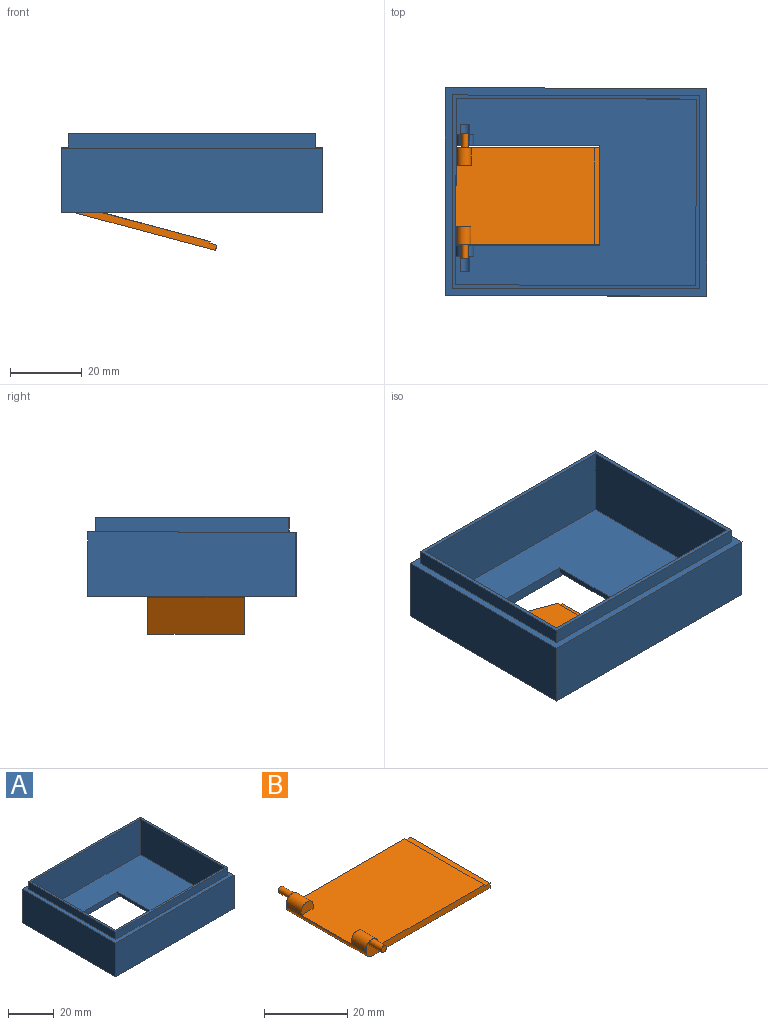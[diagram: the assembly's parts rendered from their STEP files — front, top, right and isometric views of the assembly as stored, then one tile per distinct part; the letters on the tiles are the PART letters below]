
ASSEMBLY  parts=2 mates=1
PART A: 37 faces, bbox 73x58x22 mm
  f0: plane 42x5.22mm, normal (0,-1,0), area 125mm2, adj f3,f8,f15,f16,f24,f27,f29,f31
  f1: plane 42x5.22mm, normal (0,1,0), area 125mm2, adj f2,f4,f8,f15,f16,f24,f25,f33
  f2: cylinder r=2.5mm len=3mm, axis (0,-1,0), area 8.1mm2, adj f1,f16,f26,f33
  f3: cylinder r=2.5mm len=3mm, axis (0,-1,0), area 8.1mm2, adj f0,f7,f16,f31
  f4: cylinder r=1.5mm len=7.33mm, axis (0,1,0), area 32mm2, adj f1,f5,f8,f26,f28,f33,f34
  f5: plane 2.22x1.52mm, normal (0,-1,0), area 1.8mm2, adj f4,f8,f25,f34
  f6: plane 2.22x1.52mm, normal (0,1,0), area 1.8mm2, adj f8,f27,f29,f32
  f7: plane 2.21x1.48mm, normal (0,1,0), area 1.7mm2, adj f3,f8,f29,f31
  f8: plane 67x52mm, normal (0,0,1), area 2315.2mm2, adj f0,f1,f4,f5,f6,f7,f16,f17
  f9: plane 73x18mm, normal (0,1,0), area 1314mm2, adj f12,f13,f15,f20
  f10: plane 54x4mm, normal (1,0,0), area 216mm2, adj f11,f20,f21,f23
  f11: plane 69x54mm, normal (0,0,1), area 242mm2, adj f10,f16,f17,f18,f19,f21,f22,f23
  f12: plane 58x18mm, normal (-1,0,0), area 1044mm2, adj f9,f14,f15,f20
  f13: plane 58x18mm, normal (1,0,0), area 1044mm2, adj f9,f14,f15,f20
  f14: plane 73x18mm, normal (0,-1,0), area 1314mm2, adj f12,f13,f15,f20
  f15: plane 73x58mm, normal (0,0,-1), area 3058mm2, adj f0,f1,f9,f12,f13,f14,f16,f24
  f16: plane 52x22mm, normal (1,0,0), area 1072mm2, adj f0,f1,f2,f3,f8,f11,f15,f17
  f17: plane 67x19mm, normal (0,1,0), area 1273mm2, adj f8,f11,f16,f18
  f18: plane 52x19mm, normal (-1,0,0), area 988mm2, adj f8,f11,f17,f19
  f19: plane 67x19mm, normal (0,-1,0), area 1273mm2, adj f8,f11,f16,f18
  f20: plane 73x58mm, normal (0,0,1), area 508mm2, adj f9,f10,f12,f13,f14,f21,f22,f23
  f21: plane 69x4mm, normal (0,-1,0), area 276mm2, adj f10,f11,f20,f22
  f22: plane 54x4mm, normal (-1,0,0), area 216mm2, adj f11,f20,f21,f23
  f23: plane 69x4mm, normal (0,1,0), area 276mm2, adj f10,f11,f20,f22
  f24: plane 28x1.5mm, normal (-1,0,0), area 42mm2, adj f0,f1,f15,f35
  f25: cylinder r=2.5mm len=3mm, axis (0,-1,0), area 8.2mm2, adj f1,f5,f8,f34
  f26: plane 2.21x1.48mm, normal (0,-1,0), area 1.7mm2, adj f2,f4,f8,f33
  f27: cylinder r=2.5mm len=3mm, axis (0,-1,0), area 8.2mm2, adj f0,f6,f8,f32
  f28: plane 2.61x0.76mm, normal (0,1,0), area 1.4mm2, adj f4,f8
  f29: cylinder r=1.5mm len=5.88mm, axis (0,-1,0), area 27.5mm2, adj f0,f6,f7,f8,f30,f31,f32
  f30: plane 2.61x0.76mm, normal (0,-1,0), area 1.4mm2, adj f8,f29
  f31: extruded ~3x0.79mm, area 2.7mm2, adj f0,f3,f7,f29
  f32: extruded ~3x0.8mm, area 2.7mm2, adj f0,f6,f27,f29
  f33: extruded ~3x0.79mm, area 2.7mm2, adj f1,f2,f4,f26
  f34: extruded ~3x0.8mm, area 2.7mm2, adj f1,f4,f5,f25
  f35: plane 28x2mm, normal (0,0,-1), area 56mm2, adj f0,f1,f24,f36
  f36: plane 28x1.5mm, normal (-1,0,0), area 42mm2, adj f0,f1,f8,f35
PART B: 19 faces, bbox 42x35x5 mm
  f0: plane 42x5mm, normal (0,1,0), area 89.9mm2, adj f1,f3,f4,f5,f11,f14,f15,f16
  f1: plane 40x27mm, normal (0,0,1), area 1040mm2, adj f0,f2,f4,f5,f6,f7,f8,f16
  f2: plane 42x5mm, normal (0,-1,0), area 89.9mm2, adj f1,f3,f5,f7,f9,f13,f15,f16
  f3: plane 40.03x27mm, normal (0,0,-1), area 1080.7mm2, adj f0,f2,f15,f18
  f4: plane 5x1mm, normal (1,0,0), area 5mm2, adj f0,f1,f6,f14
  f5: plane 27x1.03mm, normal (-1,0,0), area 10.7mm2, adj f0,f1,f2,f6,f8,f13,f14,f15
  f6: plane 4x3mm, normal (0,-1,0), area 10.3mm2, adj f1,f4,f5,f14
  f7: plane 5x1mm, normal (1,0,0), area 5mm2, adj f1,f2,f8,f13
  f8: plane 4x3mm, normal (0,1,0), area 10.3mm2, adj f1,f5,f7,f13
  f9: cylinder r=0.9mm len=4mm, axis (0,1,0), area 22.6mm2, adj f2,f10
  f10: plane 1.8x1.8mm, normal (0,-1,0), area 2.5mm2, adj f9
  f11: cylinder r=0.9mm len=4mm, axis (0,-1,0), area 22.6mm2, adj f0,f12
  f12: plane 1.8x1.8mm, normal (0,1,0), area 2.5mm2, adj f11
  f13: cylinder r=2mm len=5mm, axis (0,-1,0), area 31.4mm2, adj f2,f5,f7,f8
  f14: cylinder r=2mm len=5mm, axis (0,-1,0), area 31.4mm2, adj f0,f4,f5,f6
  f15: cylinder r=1.97mm len=27mm, axis (0,1,0), area 83.7mm2, adj f0,f2,f3,f5
  f16: plane 27x0.5mm, normal (1,0,0), area 13.5mm2, adj f0,f1,f2,f17
  f17: plane 27x2mm, normal (0,0,1), area 54mm2, adj f0,f2,f16,f18
  f18: plane 27x1.5mm, normal (1,0,0), area 40.5mm2, adj f0,f2,f3,f17
PLACE A rot(axis=(0.36,-0.04,-0.93),0.1deg) t=(-22.68,-19.03,-6.11)mm
PLACE B rot(axis=(0,1,-0.01),15deg) t=(-37.38,-20.16,-21.99)mm
MATE revolute B.f9 <-> A.f4  axis (0,-1,0) through (-53.74,-37.63,-13.38)mm
